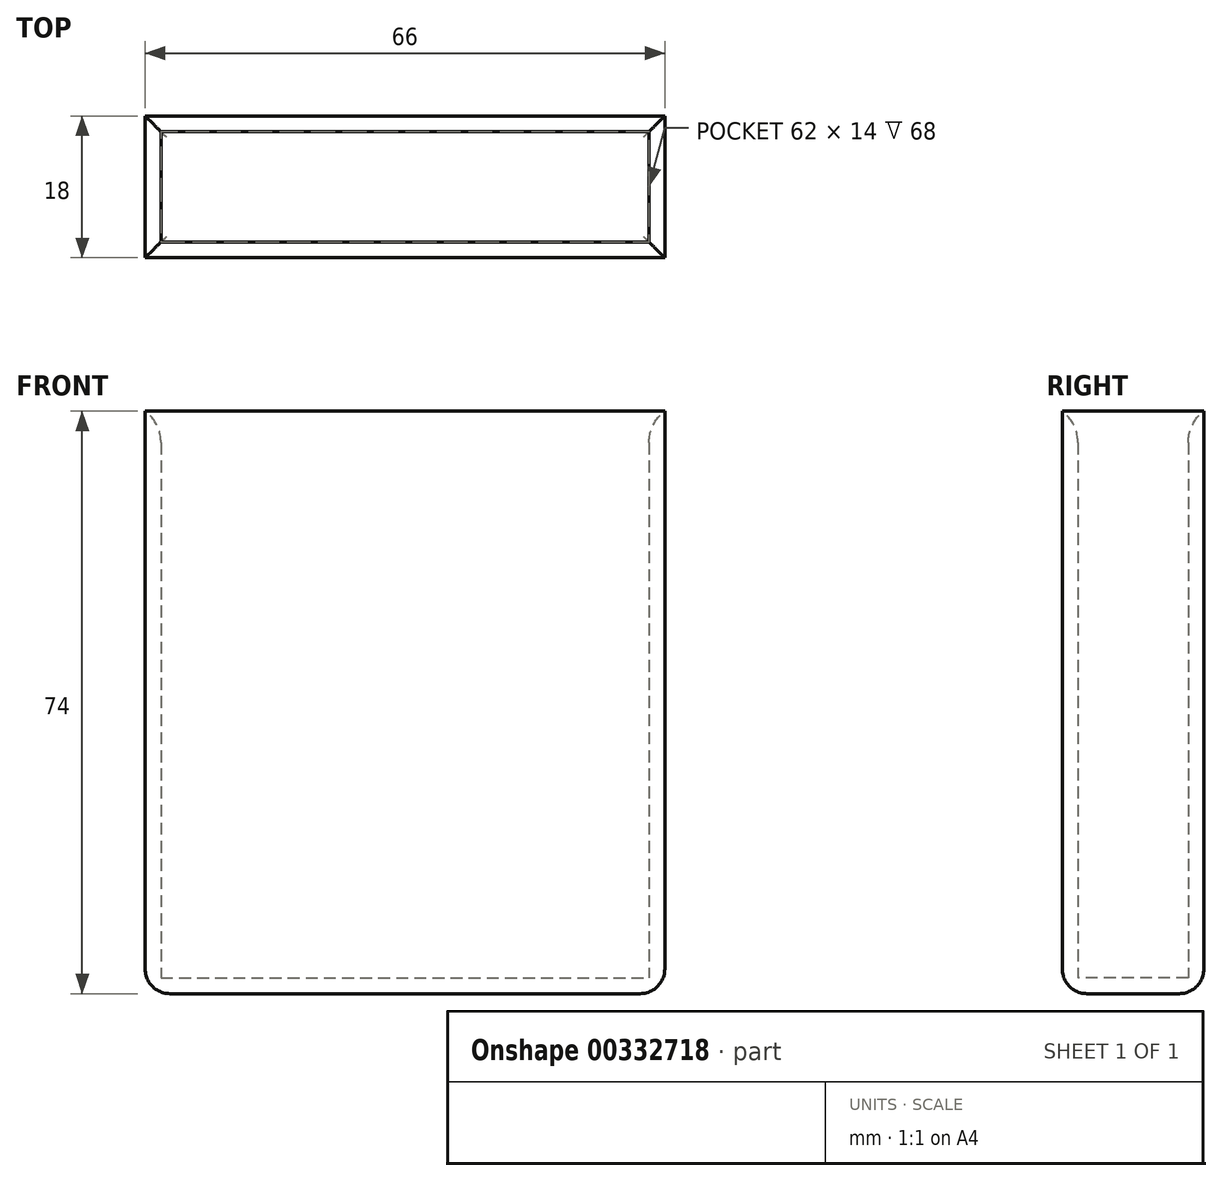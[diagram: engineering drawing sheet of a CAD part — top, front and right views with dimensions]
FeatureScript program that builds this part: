
annotation { "Feature Type Name" : "Feature", "Feature Type Description" : "" }
export const myFeature = defineFeature(function(context is Context, id is Id, definition is map)
    precondition{}
    {
        {
            var Q0;
            Q0=qCreatedBy(makeId("Top.planeOp"),FACE);
            var sketch = newSketch(context, id + "F0", { "sketchPlane" : qUnion([Q0])});
            skLineSegment(sketch, "E0.bottom", {"start": v(-26.24, 0.6) * mm, "end": v(35.76, 0.6) * mm});
            skLineSegment(sketch, "E0.top", {"start": v(-26.24, -13.4) * mm, "end": v(35.76, -13.4) * mm});
            skLineSegment(sketch, "E0.left", {"start": v(-26.24, 0.6) * mm, "end": v(-26.24, -13.4) * mm});
            skLineSegment(sketch, "E0.right", {"start": v(35.76, 0.6) * mm, "end": v(35.76, -13.4) * mm});
            skSolve(sketch);
        }
        {
            var Q0;
            Q0=makeQuery(id+"F0.imprint","IMPRINT",FACE,{"disambiguationData":[TD([[makeQuery(id+"F0.imprint","IMPRINT",EDGE,{"derivedFrom":sQuery(id+"F0.wireOp",EDGE,"E0.bottom")}),-1.0]])]});
            extrude(context, id + "F1", {"entities" : qUnion([Q0]), "depth" : 73 * mm});
        }
        {
            var Q0;
            Q0=makeQuery(id+"F1.opExtrude","CAP_FACE",FACE,{"disambiguationData":[OSD([sQuery(id+"F0.wireOp",EDGE,"E0.bottom"),sQuery(id+"F0.wireOp",EDGE,"E0.top"),sQuery(id+"F0.wireOp",EDGE,"E0.left"),sQuery(id+"F0.wireOp",EDGE,"E0.right")])],"isStart":false});
            shell(context, id + "F2", {"entities" : qUnion([Q0]), "thickness" : 2 * mm, "oppositeDirection" : true});
        }
        {
            var Q0;
            Q0=makeQuery(id+"F1.opExtrude","CAP_EDGE",EDGE,{"disambiguationData":[OSD([sQuery(id+"F0.wireOp",EDGE,"E0.right")])],"isStart":true});
            var Q1;
            Q1=makeQuery(id+"F1.opExtrude","CAP_EDGE",EDGE,{"disambiguationData":[OSD([sQuery(id+"F0.wireOp",EDGE,"E0.left")])],"isStart":true});
            var Q2;
            Q2=makeQuery(id+"F1.opExtrude","CAP_EDGE",EDGE,{"disambiguationData":[OSD([sQuery(id+"F0.wireOp",EDGE,"E0.bottom")])],"isStart":true});
            var Q3;
            Q3=makeQuery(id+"F1.opExtrude","CAP_EDGE",EDGE,{"disambiguationData":[OSD([sQuery(id+"F0.wireOp",EDGE,"E0.top")])],"isStart":true});
            fillet(context, id + "F3", {"entities" : qUnion([Q0, Q1, Q2, Q3]), "radius" : 3.14 * mm, "tangentPropagation" : true, "allowEdgeOverflow" : false});
        }
        {
            var Q0;
            {var subQ0=sQuery(id+"F0.wireOp",EDGE,"E0.right");Q0=makeQuery(id+"F2.opShell","OFFSET_EDGE",EDGE,{"disambiguationData":[OSD([subQ0]),TDD([makeQuery(id+"F1.opExtrude","CAP_EDGE",EDGE,{"disambiguationData":[OSD([subQ0])],"isStart":false})])]});}
            var Q1;
            {var subQ0=sQuery(id+"F0.wireOp",EDGE,"E0.top");Q1=makeQuery(id+"F2.opShell","OFFSET_EDGE",EDGE,{"disambiguationData":[OSD([subQ0]),TDD([makeQuery(id+"F1.opExtrude","CAP_EDGE",EDGE,{"disambiguationData":[OSD([subQ0])],"isStart":false})])]});}
            var Q2;
            {var subQ0=sQuery(id+"F0.wireOp",EDGE,"E0.bottom");Q2=makeQuery(id+"F2.opShell","OFFSET_EDGE",EDGE,{"disambiguationData":[OSD([subQ0]),TDD([makeQuery(id+"F1.opExtrude","CAP_EDGE",EDGE,{"disambiguationData":[OSD([subQ0])],"isStart":false})])]});}
            var Q3;
            {var subQ0=sQuery(id+"F0.wireOp",EDGE,"E0.left");Q3=makeQuery(id+"F2.opShell","OFFSET_EDGE",EDGE,{"disambiguationData":[OSD([subQ0]),TDD([makeQuery(id+"F1.opExtrude","CAP_EDGE",EDGE,{"disambiguationData":[OSD([subQ0])],"isStart":false})])]});}
            fillet(context, id + "F4", {"entities" : qUnion([Q0, Q1, Q2, Q3]), "radius" : 5 * mm, "tangentPropagation" : true, "allowEdgeOverflow" : false});
        }
    });
